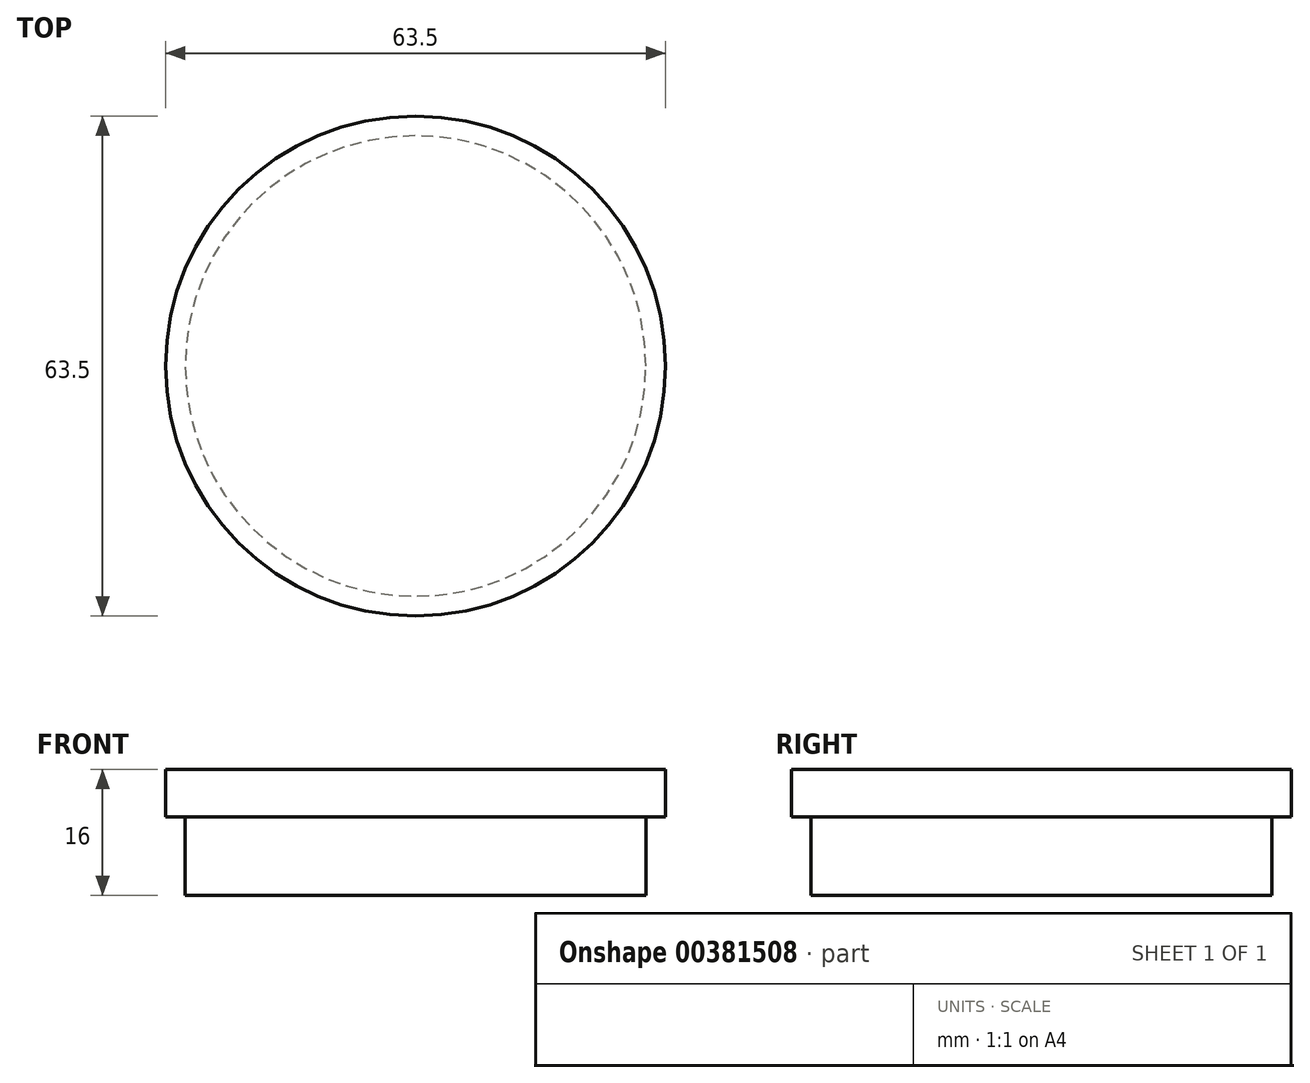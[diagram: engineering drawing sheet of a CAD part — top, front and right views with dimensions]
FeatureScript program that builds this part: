
annotation { "Feature Type Name" : "Feature", "Feature Type Description" : "" }
export const myFeature = defineFeature(function(context is Context, id is Id, definition is map)
    precondition{}
    {
        {
            var Q0;
            Q0=qCreatedBy(makeId("Front.planeOp"),FACE);
            var sketch = newSketch(context, id + "F0", { "sketchPlane" : qUnion([Q0])});
            skLineSegment(sketch, "E0", {"start": v(0, 0) * mm, "end": v(-29.25, 0) * mm});
            skLineSegment(sketch, "E1", {"start": v(-29.25, 0) * mm, "end": v(-29.25, 10) * mm});
            skLineSegment(sketch, "E2", {"start": v(-29.25, 10) * mm, "end": v(-31.75, 10) * mm});
            skLineSegment(sketch, "E3", {"start": v(-31.75, 10) * mm, "end": v(-31.75, 16) * mm});
            skLineSegment(sketch, "E4", {"start": v(-31.75, 16) * mm, "end": v(0, 16) * mm});
            skLineSegment(sketch, "E5", {"start": v(0, 16) * mm, "end": v(0, 0) * mm});
            skSolve(sketch);
        }
        {
            var Q0;
            Q0=makeQuery(id+"F0.imprint","IMPRINT",FACE,{"disambiguationData":[TD([[makeQuery(id+"F0.imprint","IMPRINT",EDGE,{"derivedFrom":sQuery(id+"F0.wireOp",EDGE,"E0")}),-1.0]])]});
            var Q1;
            Q1=sQuery(id+"F0.wireOp",EDGE,"E5");
            revolve(context, id + "F1", {"entities" : qUnion([Q0]), "axis" : qUnion([Q1]), "revolveType" : RevolveType.FULL});
        }
    });
